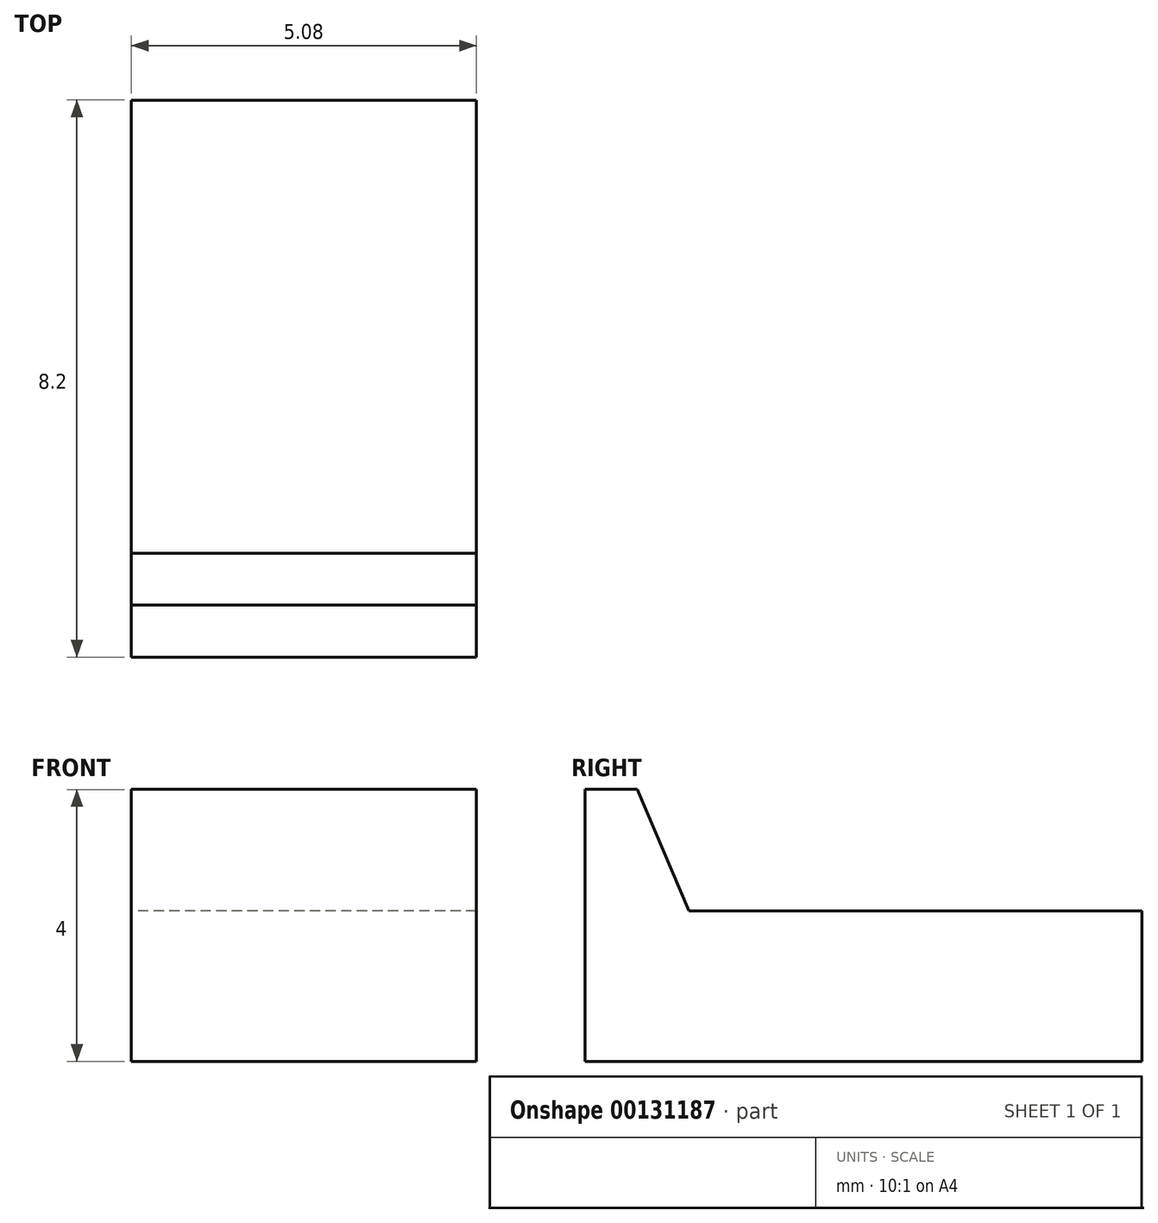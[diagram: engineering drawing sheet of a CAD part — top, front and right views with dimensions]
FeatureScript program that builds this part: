
annotation { "Feature Type Name" : "Feature", "Feature Type Description" : "" }
export const myFeature = defineFeature(function(context is Context, id is Id, definition is map)
    precondition{}
    {
        {
            var Q0;
            Q0=qCreatedBy(makeId("Right.planeOp"),FACE);
            var sketch = newSketch(context, id + "F0", { "sketchPlane" : qUnion([Q0])});
            skLineSegment(sketch, "E0.bottom", {"start": v(0, 0) * mm, "end": v(8.2, 0) * mm});
            skLineSegment(sketch, "E0.top", {"start": v(1.53, 2.21) * mm, "end": v(8.2, 2.21) * mm});
            skLineSegment(sketch, "E0.left", {"start": v(0, 0) * mm, "end": v(0, 2.21) * mm});
            skLineSegment(sketch, "E0.right", {"start": v(8.2, 0) * mm, "end": v(8.2, 2.21) * mm});
            skLineSegment(sketch, "E1.top", {"start": v(0, 4) * mm, "end": v(0.77, 4) * mm});
            skLineSegment(sketch, "E1.left", {"start": v(0, 2.21) * mm, "end": v(0, 4) * mm});
            skLineSegment(sketch, "E2", {"start": v(1.53, 2.21) * mm, "end": v(0.77, 4) * mm});
            skPoint(sketch, "E1.right.end.orphan", {"position": v(1.53, 4) * mm});
            skSolve(sketch);
        }
        {
            var Q0;
            Q0=makeQuery(id+"F0.imprint","IMPRINT",FACE,{"disambiguationData":[TD([[makeQuery(id+"F0.imprint","IMPRINT",EDGE,{"derivedFrom":sQuery(id+"F0.wireOp",EDGE,"E0.bottom")}),1.0]])]});
            extrude(context, id + "F1", {"entities" : qUnion([Q0]), "depth" : 5.08 * mm});
        }
    });
